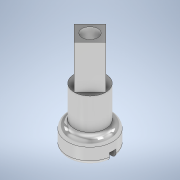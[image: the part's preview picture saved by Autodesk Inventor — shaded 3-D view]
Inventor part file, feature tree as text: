
AUTODESK INVENTOR PART (.ipt)
format: ipt  version: 2022 (Build 260153000, 153)  size: 161,280 bytes
history: native  units: mm
features: extrude x5, sketch x5, fillet x2
ambient origin geometry x8: Origin, YZ Plane, XZ Plane, XY Plane, X Axis, Y Axis, Z Axis, Center Point
bodies: Solid1 (feature_tree)
feature tree (12):
  extrude  "Extrusion1"  Depth=3.0mm TaperAngle=0.0deg
  extrude  "Extrusion2"  Depth=4.0mm TaperAngle=0.0deg
  extrude  "Extrusion3"  Depth=1.0mm
  fillet  "Fillet1"  Radius=0.5mm
  fillet  "Fillet2"  Radius=0.4mm
  extrude  "Extrusion4"  Depth=1.0mm TaperAngle=0.0deg
  extrude  "Extrusion5"  Depth=11.0mm TaperAngle=0.0deg
  sketch  "Sketch1"  dims[d0=5.8mm d1=3.0mm d2=0.0mm]
  sketch  "Sketch2"  dims[d3=4.0mm d4=4.0mm d5=0.0mm]
  sketch  "Sketch3"  dims[d6=5.5mm d7=0.0mm d8=1.0mm d9=0.5mm d10=0.4mm]
  sketch  "Sketch4"  dims[d11=0.4mm d12=1.0mm d13=0.0mm]
  sketch  "Sketch5"  dims[d14=2.0mm d15=11.0mm d16=0.0mm]
